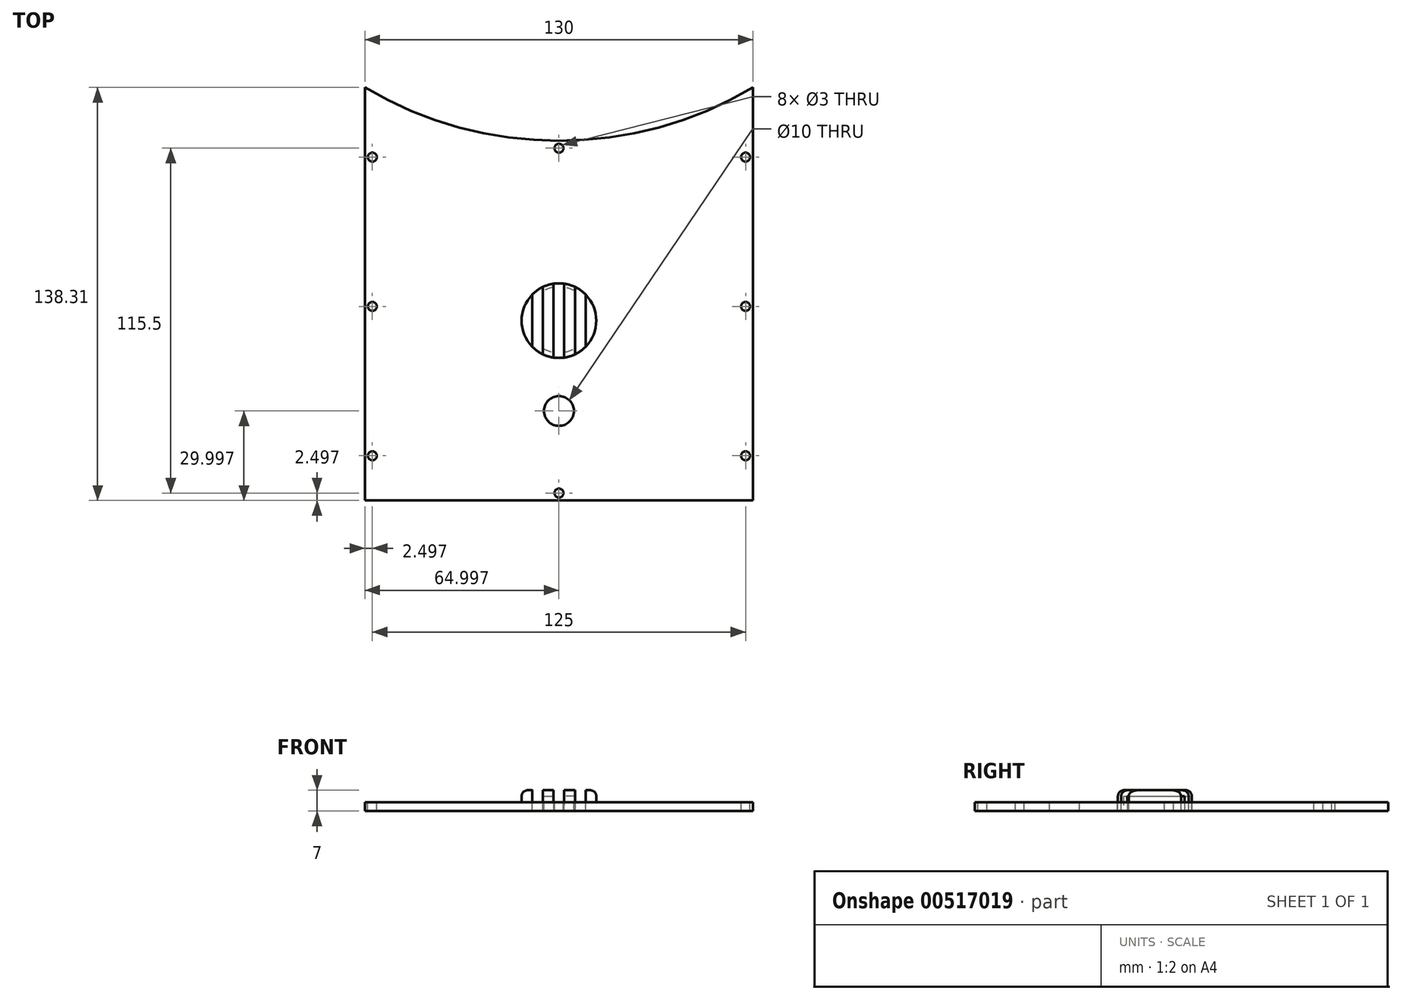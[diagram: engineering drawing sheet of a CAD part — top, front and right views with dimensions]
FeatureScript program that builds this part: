
annotation { "Feature Type Name" : "Feature", "Feature Type Description" : "" }
export const myFeature = defineFeature(function(context is Context, id is Id, definition is map)
    precondition{}
    {
        {
            var Q0;
            Q0=qCreatedBy(makeId("Top.planeOp"),FACE);
            var sketch = newSketch(context, id + "F0", { "sketchPlane" : qUnion([Q0])});
            skArc(sketch, "E0", {"start": v(-69.08, 46.8) * mm, "mid": v(-4.08, 29) * mm, "end": v(60.92, 46.8) * mm});
            skLineSegment(sketch, "E1", {"start": v(-69.08, -91.5) * mm, "end": v(60.92, -91.5) * mm});
            skLineSegment(sketch, "E2", {"start": v(60.92, -91.5) * mm, "end": v(60.92, 46.8) * mm});
            skLineSegment(sketch, "E3", {"start": v(-69.08, -91.5) * mm, "end": v(-69.08, 46.8) * mm});
            skLineSegment(sketch, "E4", {"start": v(52.58, 34.51) * mm, "end": v(52.58, 34.51) * mm});
            skLineSegment(sketch, "E5.bottom", {"start": v(-62.58, -85) * mm, "end": v(54.42, -85) * mm});
            skLineSegment(sketch, "E5.left", {"start": v(-62.58, -85) * mm, "end": v(-62.58, 33.01) * mm});
            skLineSegment(sketch, "E5.right", {"start": v(54.42, -85) * mm, "end": v(54.42, 34.51) * mm});
            skPoint(sketch, "E6.trimOffspring.end.orphan", {"position": v(52.58, 34.51) * mm});
            skArc(sketch, "E7", {"start": v(-57.4, 33.01) * mm, "mid": v(-4.08, 22) * mm, "end": v(49.23, 33.01) * mm});
            skLineSegment(sketch, "E8", {"start": v(-62.58, 33.01) * mm, "end": v(-57.4, 33.01) * mm});
            skLineSegment(sketch, "E9", {"start": v(54.42, 33.01) * mm, "end": v(49.23, 33.01) * mm});
            skLineSegment(sketch, "E10", {"start": v(-68.08, 45.65) * mm, "end": v(60.92, -91.5) * mm});
            skLineSegment(sketch, "E11", {"start": v(60.92, 46.8) * mm, "end": v(-69.08, -91.5) * mm});
            skSolve(sketch);
        }
        {
            var Q0;
            {var subQ5=sQuery(id+"F0.wireOp",EDGE,"E9");Q0=makeQuery(id+"F0.imprint","IMPRINT",FACE,{"disambiguationData":[TD([[makeQuery(id+"F0.imprint","IMPRINT",EDGE,{"derivedFrom":subQ5}),1.0]])]});}
            var Q1;
            {var subQ1=sQuery(id+"F0.wireOp",EDGE,"E5.bottom");Q1=makeQuery(id+"F0.imprint","IMPRINT",FACE,{"disambiguationData":[TD([[makeQuery(id+"F0.imprint","IMPRINT",EDGE,{"derivedFrom":subQ1}),1.0]])]});}
            var Q2;
            {var subQ0=sQuery(id+"F0.wireOp",EDGE,"E8");Q2=makeQuery(id+"F0.imprint","IMPRINT",FACE,{"disambiguationData":[TD([[makeQuery(id+"F0.imprint","IMPRINT",EDGE,{"derivedFrom":subQ0}),-1.0]])]});}
            var Q3;
            {var subQ0=sQuery(id+"F0.wireOp",EDGE,"E10");var subQ1=sQuery(id+"F0.wireOp",EDGE,"E7");var subQ2=makeQuery(id+"F0.imprint","INTERSECT",VERTEX,{"derivedFrom":[subQ1,subQ0]});Q3=makeQuery(id+"F0.imprint","IMPRINT",FACE,{"disambiguationData":[TD([[makeQuery(id+"F0.imprint","IMPRINT",EDGE,{"disambiguationData":[TD([[subQ2,-1.0]])],"derivedFrom":subQ1}),-1.0]])]});}
            var Q4;
            {var subQ7=sQuery(id+"F0.wireOp",EDGE,"E0");Q4=makeQuery(id+"F0.imprint","IMPRINT",FACE,{"disambiguationData":[TD([[makeQuery(id+"F0.imprint","IMPRINT",EDGE,{"derivedFrom":subQ7}),-1.0]])]});}
            var Q5;
            {var subQ4=sQuery(id+"F0.wireOp",EDGE,"E2");Q5=makeQuery(id+"F0.imprint","IMPRINT",FACE,{"disambiguationData":[TD([[makeQuery(id+"F0.imprint","IMPRINT",EDGE,{"derivedFrom":subQ4}),1.0]])]});}
            var Q6;
            {var subQ7=sQuery(id+"F0.wireOp",EDGE,"E1");Q6=makeQuery(id+"F0.imprint","IMPRINT",FACE,{"disambiguationData":[TD([[makeQuery(id+"F0.imprint","IMPRINT",EDGE,{"derivedFrom":subQ7}),1.0]])]});}
            extrude(context, id + "F1", {"entities" : qUnion([Q0, Q1, Q2, Q3, Q4, Q5, Q6]), "depth" : 3 * mm, "offsetDistance" : 25 * mm});
        }
        {
            var Q0;
            Q0=makeQuery(id+"F1.opExtrude","CAP_FACE",FACE,{"disambiguationData":[OSD([sQuery(id+"F0.wireOp",EDGE,"E0"),sQuery(id+"F0.wireOp",EDGE,"E1"),sQuery(id+"F0.wireOp",EDGE,"E2"),sQuery(id+"F0.wireOp",EDGE,"E3")])],"isStart":false});
            var sketch = newSketch(context, id + "F2", { "sketchPlane" : qUnion([Q0])});
            skCircle(sketch, "E12", {"center": v(58.42, -76.5) * mm, "radius": 1.5 * mm});
            skCircle(sketch, "E13", {"center": v(58.42, -26.5) * mm, "radius": 1.5 * mm});
            skCircle(sketch, "E14", {"center": v(58.42, 23.5) * mm, "radius": 1.5 * mm});
            skCircle(sketch, "E15", {"center": v(-4.08, 26.5) * mm, "radius": 1.5 * mm});
            skCircle(sketch, "E16", {"center": v(-66.58, -76.5) * mm, "radius": 1.5 * mm});
            skCircle(sketch, "E17", {"center": v(-4.08, -89) * mm, "radius": 1.5 * mm});
            skLineSegment(sketch, "E18", {"start": v(-69.08, -91.5) * mm, "end": v(60.92, -91.5) * mm, "construction": true});
            skLineSegment(sketch, "E19", {"start": v(-69.08, -91.5) * mm, "end": v(-69.08, 46.8) * mm, "construction": true});
            skLineSegment(sketch, "E20", {"start": v(-69.08, 26.36) * mm, "end": v(60.92, 26.36) * mm, "construction": true});
            skCircle(sketch, "E21", {"center": v(-66.58, -26.5) * mm, "radius": 1.5 * mm});
            skCircle(sketch, "E22", {"center": v(-66.58, 23.5) * mm, "radius": 1.5 * mm});
            skSolve(sketch);
        }
        {
            var Q0;
            Q0 = qSketchRegion(id + "F2", true);
            extrude(context, id + "F3", {"entities" : qUnion([Q0]), "operationType" : NewBodyOperationType.REMOVE, "oppositeDirection" : true, "depth" : 25 * mm, "offsetDistance" : 25 * mm});
        }
        {
            var Q0;
            Q0=makeQuery(id+"F1.opExtrude","CAP_FACE",FACE,{"disambiguationData":[OSD([sQuery(id+"F0.wireOp",EDGE,"E0"),sQuery(id+"F0.wireOp",EDGE,"E1"),sQuery(id+"F0.wireOp",EDGE,"E2"),sQuery(id+"F0.wireOp",EDGE,"E3")])],"isStart":false});
            var sketch = newSketch(context, id + "F4", { "sketchPlane" : qUnion([Q0])});
            skLineSegment(sketch, "E23", {"start": v(-4.08, 26.5) * mm, "end": v(-4.08, -89) * mm, "construction": true});
            skCircle(sketch, "E24", {"center": v(-4.08, -31.25) * mm, "radius": 12.5 * mm});
            skLineSegment(sketch, "E25", {"start": v(-9.44, -19.96) * mm, "end": v(-9.44, -42.55) * mm});
            skLineSegment(sketch, "E26", {"start": v(-5.87, -18.88) * mm, "end": v(-5.87, -43.63) * mm});
            skLineSegment(sketch, "E27", {"start": v(-2.3, -18.88) * mm, "end": v(-2.3, -43.63) * mm});
            skLineSegment(sketch, "E28", {"start": v(4.85, -22.5) * mm, "end": v(4.85, -40) * mm});
            skLineSegment(sketch, "E29", {"start": v(-13.01, -22.5) * mm, "end": v(-13.01, -40) * mm});
            skLineSegment(sketch, "E30", {"start": v(-14.17, -31.25) * mm, "end": v(7.5, -31.25) * mm, "construction": true});
            skLineSegment(sketch, "E31", {"start": v(1.27, -19.96) * mm, "end": v(1.27, -42.55) * mm});
            skCircle(sketch, "E32", {"center": v(-4.08, -61.5) * mm, "radius": 5 * mm});
            skSolve(sketch);
        }
        {
            var Q0;
            {var subQ0=sQuery(id+"F4.wireOp",EDGE,"E29");Q0=makeQuery(id+"F4.imprint","IMPRINT",FACE,{"disambiguationData":[TD([[makeQuery(id+"F4.imprint","IMPRINT",EDGE,{"derivedFrom":subQ0}),-1.0]])]});}
            var Q1;
            {var subQ0=sQuery(id+"F4.wireOp",EDGE,"E28");Q1=makeQuery(id+"F4.imprint","IMPRINT",FACE,{"disambiguationData":[TD([[makeQuery(id+"F4.imprint","IMPRINT",EDGE,{"derivedFrom":subQ0}),1.0]])]});}
            var Q2;
            {var subQ0=sQuery(id+"F4.wireOp",EDGE,"E27");Q2=makeQuery(id+"F4.imprint","IMPRINT",FACE,{"disambiguationData":[TD([[makeQuery(id+"F4.imprint","IMPRINT",EDGE,{"derivedFrom":subQ0}),1.0]])]});}
            var Q3;
            {var subQ0=sQuery(id+"F4.wireOp",EDGE,"E25");Q3=makeQuery(id+"F4.imprint","IMPRINT",FACE,{"disambiguationData":[TD([[makeQuery(id+"F4.imprint","IMPRINT",EDGE,{"derivedFrom":subQ0}),1.0]])]});}
            extrude(context, id + "F5", {"entities" : qUnion([Q0, Q1, Q2, Q3]), "operationType" : NewBodyOperationType.ADD, "depth" : 4 * mm, "offsetDistance" : 25 * mm});
        }
        {
            var Q0;
            {var subQ0=sQuery(id+"F4.wireOp",EDGE,"E25");Q0=makeQuery(id+"F4.imprint","IMPRINT",FACE,{"disambiguationData":[TD([[makeQuery(id+"F4.imprint","IMPRINT",EDGE,{"derivedFrom":subQ0}),-1.0]])]});}
            var Q1;
            {var subQ0=sQuery(id+"F4.wireOp",EDGE,"E26");Q1=makeQuery(id+"F4.imprint","IMPRINT",FACE,{"disambiguationData":[TD([[makeQuery(id+"F4.imprint","IMPRINT",EDGE,{"derivedFrom":subQ0}),1.0]])]});}
            var Q2;
            {var subQ0=sQuery(id+"F4.wireOp",EDGE,"E28");Q2=makeQuery(id+"F4.imprint","IMPRINT",FACE,{"disambiguationData":[TD([[makeQuery(id+"F4.imprint","IMPRINT",EDGE,{"derivedFrom":subQ0}),-1.0]])]});}
            extrude(context, id + "F6", {"entities" : qUnion([Q0, Q1, Q2]), "operationType" : NewBodyOperationType.REMOVE, "oppositeDirection" : true, "depth" : 25 * mm, "offsetDistance" : 25 * mm});
        }
        {
            var Q0;
            {var subQ0=sQuery(id+"F4.wireOp",EDGE,"E24");Q0=makeQuery(id+"F5.opExtrude","CAP_EDGE",EDGE,{"disambiguationData":[OSD([subQ0]),TDD([makeQuery(id+"F4.imprint","IMPRINT",EDGE,{"disambiguationData":[TD([[makeQuery(id+"F4.imprint","INTERSECT",VERTEX,{"disambiguationData":[OD(0.0)],"derivedFrom":[subQ0,sQuery(id+"F4.wireOp",EDGE,"E25")]}),1.0]])],"derivedFrom":subQ0})])],"isStart":false});}
            var Q1;
            {var subQ0=sQuery(id+"F4.wireOp",EDGE,"E29");var subQ1=sQuery(id+"F4.wireOp",EDGE,"E24");Q1=makeQuery(id+"F5.opExtrude","CAP_EDGE",EDGE,{"disambiguationData":[OSD([subQ1]),TDD([makeQuery(id+"F4.imprint","IMPRINT",EDGE,{"disambiguationData":[TD([[makeQuery(id+"F4.imprint","INTERSECT",VERTEX,{"disambiguationData":[OD(0.0)],"derivedFrom":[subQ1,subQ0]}),-1.0]])],"derivedFrom":subQ1})])],"isStart":false});}
            var Q2;
            {var subQ0=sQuery(id+"F4.wireOp",EDGE,"E24");Q2=makeQuery(id+"F5.opExtrude","CAP_EDGE",EDGE,{"disambiguationData":[OSD([subQ0]),TDD([makeQuery(id+"F4.imprint","IMPRINT",EDGE,{"disambiguationData":[TD([[makeQuery(id+"F4.imprint","INTERSECT",VERTEX,{"disambiguationData":[OD(0.0)],"derivedFrom":[subQ0,sQuery(id+"F4.wireOp",EDGE,"E27")]}),1.0]])],"derivedFrom":subQ0})])],"isStart":false});}
            var Q3;
            {var subQ0=sQuery(id+"F4.wireOp",EDGE,"E28");var subQ1=sQuery(id+"F4.wireOp",EDGE,"E24");Q3=makeQuery(id+"F5.opExtrude","CAP_EDGE",EDGE,{"disambiguationData":[OSD([subQ1]),TDD([makeQuery(id+"F4.imprint","IMPRINT",EDGE,{"disambiguationData":[TD([[makeQuery(id+"F4.imprint","INTERSECT",VERTEX,{"disambiguationData":[OD(0.0)],"derivedFrom":[subQ1,subQ0]}),1.0]])],"derivedFrom":subQ1})])],"isStart":false});}
            var Q4;
            {var subQ0=sQuery(id+"F4.wireOp",EDGE,"E24");Q4=makeQuery(id+"F5.opExtrude","CAP_EDGE",EDGE,{"disambiguationData":[OSD([subQ0]),TDD([makeQuery(id+"F4.imprint","IMPRINT",EDGE,{"disambiguationData":[TD([[makeQuery(id+"F4.imprint","INTERSECT",VERTEX,{"disambiguationData":[OD(1.0)],"derivedFrom":[subQ0,sQuery(id+"F4.wireOp",EDGE,"E27")]}),-1.0]])],"derivedFrom":subQ0})])],"isStart":false});}
            var Q5;
            {var subQ0=sQuery(id+"F4.wireOp",EDGE,"E24");Q5=makeQuery(id+"F5.opExtrude","CAP_EDGE",EDGE,{"disambiguationData":[OSD([subQ0]),TDD([makeQuery(id+"F4.imprint","IMPRINT",EDGE,{"disambiguationData":[TD([[makeQuery(id+"F4.imprint","INTERSECT",VERTEX,{"disambiguationData":[OD(1.0)],"derivedFrom":[subQ0,sQuery(id+"F4.wireOp",EDGE,"E25")]}),-1.0]])],"derivedFrom":subQ0})])],"isStart":false});}
            fillet(context, id + "F7", {"entities" : qUnion([Q0, Q1, Q2, Q3, Q4, Q5]), "radius" : 2 * mm, "tangentPropagation" : true, "allowEdgeOverflow" : false});
        }
        {
            var Q0;
            Q0=makeQuery(id+"F1.opExtrude","CAP_FACE",FACE,{"disambiguationData":[OSD([sQuery(id+"F0.wireOp",EDGE,"E0"),sQuery(id+"F0.wireOp",EDGE,"E1"),sQuery(id+"F0.wireOp",EDGE,"E2"),sQuery(id+"F0.wireOp",EDGE,"E3")])],"isStart":true});
            var sketch = newSketch(context, id + "F8", { "sketchPlane" : qUnion([Q0])});
            skLineSegment(sketch, "E33", {"start": v(-13.01, 30.95) * mm, "end": v(4.85, 30.95) * mm, "construction": true});
            skLineSegment(sketch, "E34", {"start": v(-4.08, 43.75) * mm, "end": v(-4.08, 18.75) * mm, "construction": true});
            skCircle(sketch, "E35", {"center": v(-4.08, 30.95) * mm, "radius": 11 * mm});
            skSolve(sketch);
        }
        {
            var Q0;
            {var subQ0=sQuery(id+"F8.wireOp",EDGE,"E35");var subQ1=makeQuery(id+"F6.boolean.opBoolean","INTERSECT",EDGE,{"derivedFrom":[makeQuery(id+"F1.opExtrude","CAP_FACE",FACE,{"disambiguationData":[OSD([sQuery(id+"F0.wireOp",EDGE,"E0"),sQuery(id+"F0.wireOp",EDGE,"E1"),sQuery(id+"F0.wireOp",EDGE,"E2"),sQuery(id+"F0.wireOp",EDGE,"E3")])],"isStart":true}),makeQuery(id+"F6.opExtrude","SWEPT_FACE",FACE,{"disambiguationData":[OSD([sQuery(id+"F4.wireOp",EDGE,"E25")])]})]});var subQ2=makeQuery(id+"F8.imprint","INTERSECT",VERTEX,{"disambiguationData":[OD(0.0)],"derivedFrom":[subQ1,subQ0]});Q0=makeQuery(id+"F8.imprint","IMPRINT",FACE,{"disambiguationData":[TD([[makeQuery(id+"F8.imprint","IMPRINT",EDGE,{"disambiguationData":[TD([[subQ2,-1.0]])],"derivedFrom":subQ0}),1.0]])]});}
            var Q1;
            {var subQ0=sQuery(id+"F8.wireOp",EDGE,"E35");var subQ1=makeQuery(id+"F6.boolean.opBoolean","INTERSECT",EDGE,{"derivedFrom":[makeQuery(id+"F1.opExtrude","CAP_FACE",FACE,{"disambiguationData":[OSD([sQuery(id+"F0.wireOp",EDGE,"E0"),sQuery(id+"F0.wireOp",EDGE,"E1"),sQuery(id+"F0.wireOp",EDGE,"E2"),sQuery(id+"F0.wireOp",EDGE,"E3")])],"isStart":true}),makeQuery(id+"F6.opExtrude","SWEPT_FACE",FACE,{"disambiguationData":[OSD([sQuery(id+"F4.wireOp",EDGE,"E31")])]})]});var subQ2=makeQuery(id+"F8.imprint","INTERSECT",VERTEX,{"disambiguationData":[OD(0.0)],"derivedFrom":[subQ1,subQ0]});Q1=makeQuery(id+"F8.imprint","IMPRINT",FACE,{"disambiguationData":[TD([[makeQuery(id+"F8.imprint","IMPRINT",EDGE,{"disambiguationData":[TD([[subQ2,1.0]])],"derivedFrom":subQ0}),1.0]])]});}
            var Q2;
            {var subQ0=sQuery(id+"F8.wireOp",EDGE,"E35");var subQ1=makeQuery(id+"F1.opExtrude","CAP_FACE",FACE,{"disambiguationData":[OSD([sQuery(id+"F0.wireOp",EDGE,"E0"),sQuery(id+"F0.wireOp",EDGE,"E1"),sQuery(id+"F0.wireOp",EDGE,"E2"),sQuery(id+"F0.wireOp",EDGE,"E3")])],"isStart":true});var subQ2=makeQuery(id+"F6.boolean.opBoolean","INTERSECT",EDGE,{"derivedFrom":[subQ1,makeQuery(id+"F6.opExtrude","SWEPT_FACE",FACE,{"disambiguationData":[OSD([sQuery(id+"F4.wireOp",EDGE,"E27")])]})]});var subQ3=makeQuery(id+"F8.imprint","INTERSECT",VERTEX,{"disambiguationData":[OD(0.0)],"derivedFrom":[subQ2,subQ0]});Q2=makeQuery(id+"F8.imprint","IMPRINT",FACE,{"disambiguationData":[TD([[makeQuery(id+"F8.imprint","IMPRINT",EDGE,{"disambiguationData":[TD([[subQ3,1.0]])],"derivedFrom":subQ0}),1.0]])]});}
            var Q3;
            {var subQ0=sQuery(id+"F8.wireOp",EDGE,"E35");var subQ1=makeQuery(id+"F1.opExtrude","CAP_FACE",FACE,{"disambiguationData":[OSD([sQuery(id+"F0.wireOp",EDGE,"E0"),sQuery(id+"F0.wireOp",EDGE,"E1"),sQuery(id+"F0.wireOp",EDGE,"E2"),sQuery(id+"F0.wireOp",EDGE,"E3")])],"isStart":true});var subQ2=makeQuery(id+"F6.boolean.opBoolean","INTERSECT",EDGE,{"derivedFrom":[subQ1,makeQuery(id+"F6.opExtrude","SWEPT_FACE",FACE,{"disambiguationData":[OSD([sQuery(id+"F4.wireOp",EDGE,"E26")])]})]});var subQ3=makeQuery(id+"F8.imprint","INTERSECT",VERTEX,{"disambiguationData":[OD(0.0)],"derivedFrom":[subQ2,subQ0]});Q3=makeQuery(id+"F8.imprint","IMPRINT",FACE,{"disambiguationData":[TD([[makeQuery(id+"F8.imprint","IMPRINT",EDGE,{"disambiguationData":[TD([[subQ3,-1.0]])],"derivedFrom":subQ0}),1.0]])]});}
            var Q4;
            {var subQ0=sQuery(id+"F8.wireOp",EDGE,"E35");var subQ1=makeQuery(id+"F6.boolean.opBoolean","INTERSECT",EDGE,{"derivedFrom":[makeQuery(id+"F1.opExtrude","CAP_FACE",FACE,{"disambiguationData":[OSD([sQuery(id+"F0.wireOp",EDGE,"E0"),sQuery(id+"F0.wireOp",EDGE,"E1"),sQuery(id+"F0.wireOp",EDGE,"E2"),sQuery(id+"F0.wireOp",EDGE,"E3")])],"isStart":true}),makeQuery(id+"F6.opExtrude","SWEPT_FACE",FACE,{"disambiguationData":[OSD([sQuery(id+"F4.wireOp",EDGE,"E29")])]})]});var subQ2=makeQuery(id+"F8.imprint","INTERSECT",VERTEX,{"disambiguationData":[OD(0.0)],"derivedFrom":[subQ1,subQ0]});Q4=makeQuery(id+"F8.imprint","IMPRINT",FACE,{"disambiguationData":[TD([[makeQuery(id+"F8.imprint","IMPRINT",EDGE,{"disambiguationData":[TD([[subQ2,-1.0]])],"derivedFrom":subQ0}),1.0]])]});}
            var Q5;
            {var subQ0=sQuery(id+"F8.wireOp",EDGE,"E35");var subQ1=makeQuery(id+"F6.boolean.opBoolean","INTERSECT",EDGE,{"derivedFrom":[makeQuery(id+"F1.opExtrude","CAP_FACE",FACE,{"disambiguationData":[OSD([sQuery(id+"F0.wireOp",EDGE,"E0"),sQuery(id+"F0.wireOp",EDGE,"E1"),sQuery(id+"F0.wireOp",EDGE,"E2"),sQuery(id+"F0.wireOp",EDGE,"E3")])],"isStart":true}),makeQuery(id+"F6.opExtrude","SWEPT_FACE",FACE,{"disambiguationData":[OSD([sQuery(id+"F4.wireOp",EDGE,"E28")])]})]});var subQ2=makeQuery(id+"F8.imprint","INTERSECT",VERTEX,{"disambiguationData":[OD(0.0)],"derivedFrom":[subQ1,subQ0]});Q5=makeQuery(id+"F8.imprint","IMPRINT",FACE,{"disambiguationData":[TD([[makeQuery(id+"F8.imprint","IMPRINT",EDGE,{"disambiguationData":[TD([[subQ2,1.0]])],"derivedFrom":subQ0}),1.0]])]});}
            extrude(context, id + "F9", {"entities" : qUnion([Q0, Q1, Q2, Q3, Q4, Q5]), "operationType" : NewBodyOperationType.REMOVE, "oppositeDirection" : true, "depth" : 5 * mm, "offsetDistance" : 25 * mm});
        }
        {
            var Q0;
            Q0=makeQuery(id+"F1.opExtrude","CAP_FACE",FACE,{"disambiguationData":[OSD([sQuery(id+"F0.wireOp",EDGE,"E0"),sQuery(id+"F0.wireOp",EDGE,"E1"),sQuery(id+"F0.wireOp",EDGE,"E2"),sQuery(id+"F0.wireOp",EDGE,"E3")])],"isStart":false});
            var sketch = newSketch(context, id + "F10", { "sketchPlane" : qUnion([Q0])});
            skLineSegment(sketch, "E36", {"start": v(-4.08, 26.5) * mm, "end": v(-4.08, -90.5) * mm, "construction": true});
            skCircle(sketch, "E37", {"center": v(-4.08, -61.5) * mm, "radius": 5 * mm});
            skSolve(sketch);
        }
        {
            var Q0;
            Q0=makeQuery(id+"F10.imprint","IMPRINT",FACE,{"disambiguationData":[TD([[makeQuery(id+"F10.imprint","IMPRINT",EDGE,{"derivedFrom":sQuery(id+"F10.wireOp",EDGE,"E37")}),1.0]])]});
            extrude(context, id + "F11", {"entities" : qUnion([Q0]), "operationType" : NewBodyOperationType.REMOVE, "oppositeDirection" : true, "depth" : 25 * mm, "offsetDistance" : 25 * mm});
        }
    });
